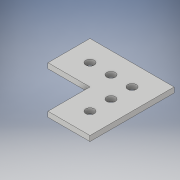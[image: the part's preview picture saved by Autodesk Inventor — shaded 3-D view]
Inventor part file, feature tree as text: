
AUTODESK INVENTOR PART (.ipt)
format: ipt  version: 2018 (Build 220112000, 112)  size: 117,248 bytes
history: native  units: in
note: dims shown in document units (in); Inventor stores cm internally (conversion verified against a paired STEP export)
features: extrude x1, sketch x1
ambient origin geometry x8: Origin, YZ Plane, XZ Plane, XY Plane, X Axis, Y Axis, Z Axis, Center Point
bodies: Solid1 (feature_tree)
feature tree (2):
  extrude  "Extrusion1"  Depth=1.0in
  sketch  "Sketch1"  dims[d0=1.0in d2=1.0in d3=1.0in d4=0.5in d5=0.5in d6=0.5in d7=0.2031in d8=0.2031in d9=0.2031in d10=0.2031in d11=0.2031in d12=0.125in d13=0.0in]
